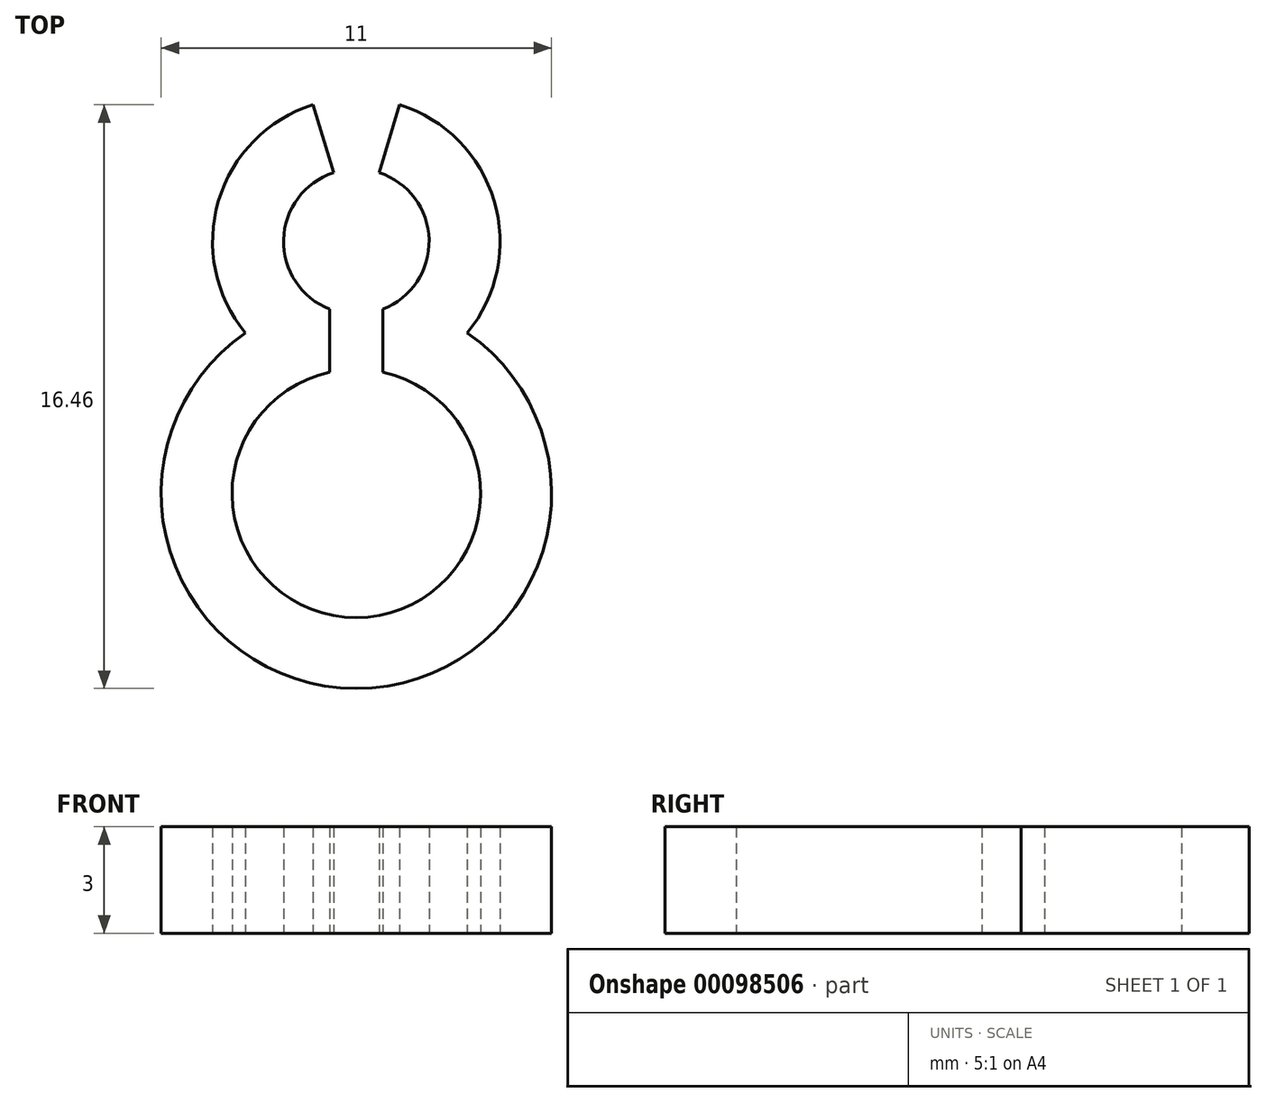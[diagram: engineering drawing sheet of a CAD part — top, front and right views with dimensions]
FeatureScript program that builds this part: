
annotation { "Feature Type Name" : "Feature", "Feature Type Description" : "" }
export const myFeature = defineFeature(function(context is Context, id is Id, definition is map)
    precondition{}
    {
        {
            var Q0;
            Q0=qCreatedBy(makeId("Top.planeOp"),FACE);
            var sketch = newSketch(context, id + "F0", { "sketchPlane" : qUnion([Q0])});
            skArc(sketch, "E0", {"start": v(-1.22, 1.65) * mm, "mid": v(-2.03, -0.27) * mm, "end": v(-0.75, -1.9) * mm});
            skArc(sketch, "E1.0", {"start": v(-1.22, 3.86) * mm, "mid": v(-3.88, 1.15) * mm, "end": v(-3.13, -2.57) * mm});
            skLineSegment(sketch, "E2", {"start": v(0, 0) * mm, "end": v(0, -7.1) * mm, "construction": true});
            skArc(sketch, "E3", {"start": v(-0.75, -3.68) * mm, "mid": v(0, -10.6) * mm, "end": v(0.75, -3.68) * mm});
            skArc(sketch, "E4.0", {"start": v(-3.13, -2.57) * mm, "mid": v(0, -12.6) * mm, "end": v(3.13, -2.57) * mm});
            skLineSegment(sketch, "E5", {"start": v(0, 0) * mm, "end": v(0, 4.05) * mm, "construction": true});
            skLineSegment(sketch, "E6", {"start": v(0, 4.05) * mm, "end": v(3, 4.05) * mm, "construction": true});
            skLineSegment(sketch, "E7", {"start": v(0, 4.05) * mm, "end": v(-3, 4.05) * mm, "construction": true});
            skPoint(sketch, "E8", {"position": v(1.22, 1.65) * mm});
            skPoint(sketch, "E9", {"position": v(-1.22, 1.65) * mm});
            skLineSegment(sketch, "E10", {"start": v(0, -3.2) * mm, "end": v(-0.75, -3.2) * mm, "construction": true});
            skLineSegment(sketch, "E11", {"start": v(0, -3.2) * mm, "end": v(0.75, -3.2) * mm, "construction": true});
            skLineSegment(sketch, "E12", {"start": v(-0.75, -3.2) * mm, "end": v(-0.75, -3.68) * mm});
            skLineSegment(sketch, "E13", {"start": v(-0.75, -3.68) * mm, "end": v(-0.75, -1.9) * mm});
            skLineSegment(sketch, "E14", {"start": v(0.75, -3.2) * mm, "end": v(0.75, -3.68) * mm});
            skLineSegment(sketch, "E15", {"start": v(0.75, -3.68) * mm, "end": v(0.75, -1.9) * mm});
            skArc(sketch, "E16.trimOffspring", {"start": v(0.75, -1.9) * mm, "mid": v(2.03, -0.27) * mm, "end": v(1.22, 1.65) * mm});
            skArc(sketch, "E17.trimOffspring", {"start": v(3.13, -2.57) * mm, "mid": v(3.88, 1.15) * mm, "end": v(1.22, 3.86) * mm});
            skArc(sketch, "E18", {"start": v(-0.64, 1.95) * mm, "mid": v(-2.05, 0.06) * mm, "end": v(-0.75, -1.9) * mm});
            skLineSegment(sketch, "E19", {"start": v(-1.22, 3.86) * mm, "end": v(-0.64, 1.95) * mm});
            skLineSegment(sketch, "E20", {"start": v(1.22, 3.86) * mm, "end": v(0.64, 1.95) * mm});
            skArc(sketch, "E21.trimOffspring", {"start": v(0.75, -1.9) * mm, "mid": v(2.05, 0.06) * mm, "end": v(0.64, 1.95) * mm});
            skSolve(sketch);
        }
        {
            var Q0;
            Q0=makeQuery(id+"F0.imprint","IMPRINT",FACE,{"disambiguationData":[TD([[makeQuery(id+"F0.imprint","IMPRINT",EDGE,{"derivedFrom":sQuery(id+"F0.wireOp",EDGE,"E1.0")}),1.0]])]});
            extrude(context, id + "F1", {"entities" : qUnion([Q0]), "depth" : 3 * mm});
        }
    });
